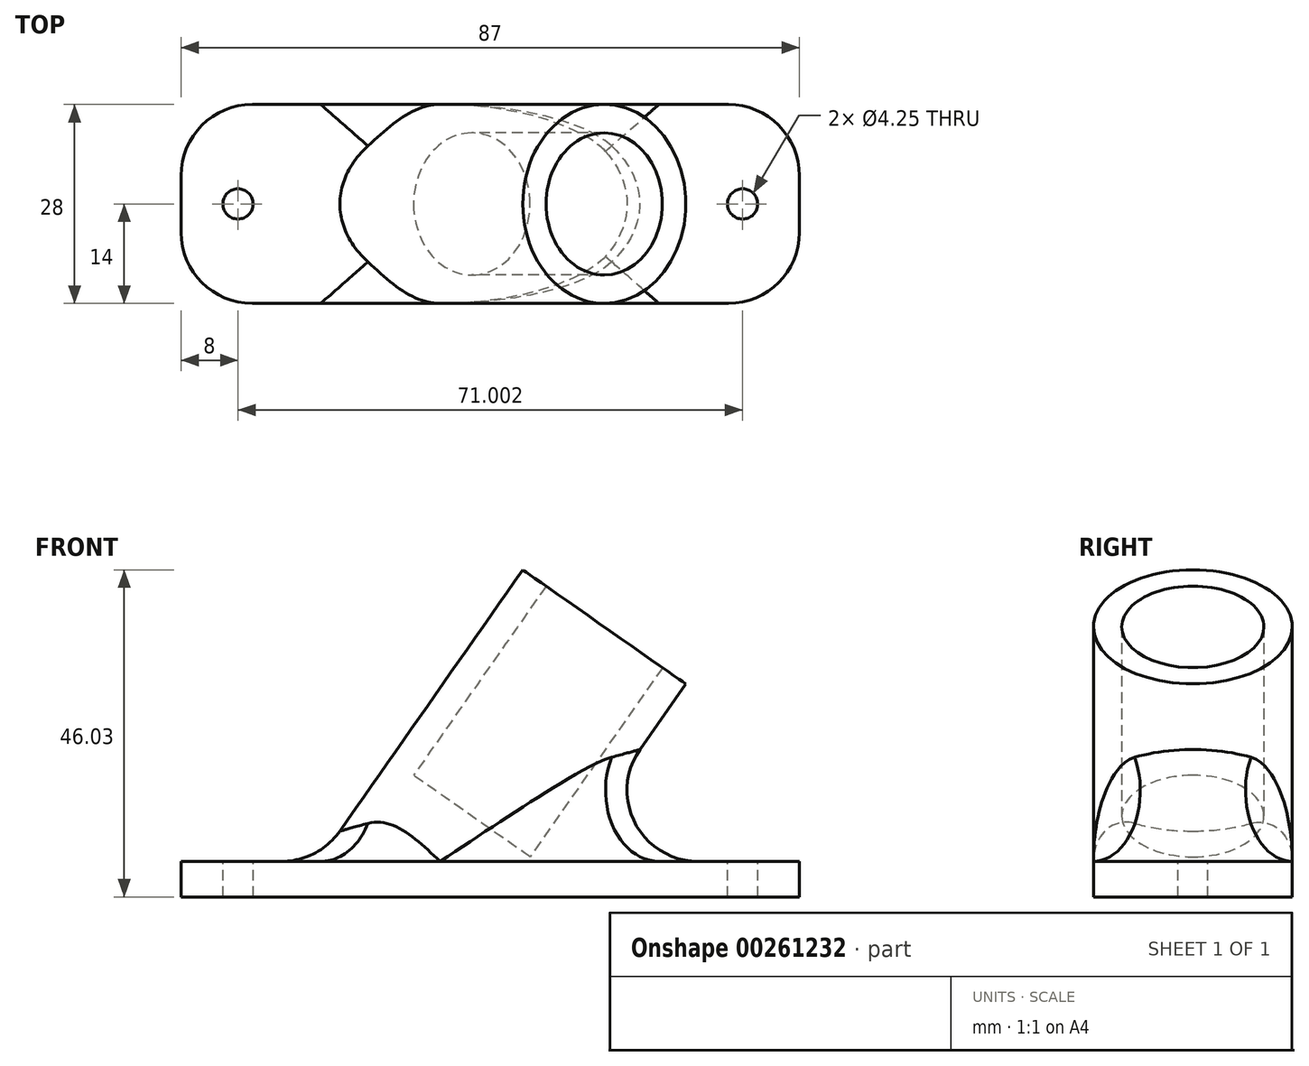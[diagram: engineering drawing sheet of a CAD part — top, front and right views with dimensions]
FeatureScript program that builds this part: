
annotation { "Feature Type Name" : "Feature", "Feature Type Description" : "" }
export const myFeature = defineFeature(function(context is Context, id is Id, definition is map)
    precondition{}
    {
        {
            var Q0;
            Q0=qCreatedBy(makeId("Front.planeOp"),FACE);
            var sketch = newSketch(context, id + "F0", { "sketchPlane" : qUnion([Q0])});
            skPoint(sketch, "E0", {"position": v(-30, 0) * mm});
            skPoint(sketch, "E1", {"position": v(30, 0) * mm});
            skLineSegment(sketch, "E2", {"start": v(-30, 0) * mm, "end": v(30, 0) * mm, "construction": true});
            skLineSegment(sketch, "E3", {"start": v(0, 0) * mm, "end": v(30.9, 44.14) * mm, "construction": true});
            skLineSegment(sketch, "E4", {"start": v(0, 0) * mm, "end": v(0, 38) * mm, "construction": true});
            skLineSegment(sketch, "E5", {"start": v(0, 38) * mm, "end": v(26.6, 38) * mm, "construction": true});
            skPoint(sketch, "E6", {"position": v(26.6, 38) * mm});
            skSolve(sketch);
        }
        {
            var Q0;
            Q0=qCreatedBy(makeId("Front.planeOp"),FACE);
            var sketch = newSketch(context, id + "F1", { "sketchPlane" : qUnion([Q0])});
            skLineSegment(sketch, "E7.0", {"start": v(-30, 0) * mm, "end": v(30, 0) * mm});
            skPoint(sketch, "E8.0", {"position": v(26.6, 38) * mm});
            skLineSegment(sketch, "E9", {"start": v(26.6, 38) * mm, "end": v(38.08, 29.97) * mm, "construction": true});
            skLineSegment(sketch, "E10", {"start": v(26.6, 38) * mm, "end": v(15.14, 46.03) * mm, "construction": true});
            skLineSegment(sketch, "E11", {"start": v(0, 0) * mm, "end": v(0, 5) * mm});
            skLineSegment(sketch, "E12", {"start": v(15.14, 46.03) * mm, "end": v(18.42, 43.74) * mm});
            skLineSegment(sketch, "E13", {"start": v(18.42, 43.74) * mm, "end": v(-15.51, -4.72) * mm});
            skLineSegment(sketch, "E14", {"start": v(-15.51, -4.72) * mm, "end": v(-18.79, -2.42) * mm});
            skLineSegment(sketch, "E15", {"start": v(-18.79, -2.42) * mm, "end": v(15.14, 46.03) * mm});
            skLineSegment(sketch, "E16.0", {"start": v(0, 0) * mm, "end": v(30.9, 44.14) * mm});
            skSolve(sketch);
        }
        {
            var Q0;
            Q0 = qSketchRegion(id + "F1", true);
            var Q1;
            Q1=sQuery(id+"F1.wireOp",EDGE,"E16.0");
            revolve(context, id + "F2", {"entities" : qUnion([Q0]), "axis" : qUnion([Q1]), "revolveType" : RevolveType.FULL});
        }
        {
            var Q0;
            Q0=qCreatedBy(makeId("Top.planeOp"),FACE);
            var sketch = newSketch(context, id + "F3", { "sketchPlane" : qUnion([Q0])});
            skLineSegment(sketch, "E17", {"start": v(38.07, 0) * mm, "end": v(54.07, 0) * mm});
            skLineSegment(sketch, "E18", {"start": v(-16.93, 0) * mm, "end": v(-32.93, 0) * mm});
            skLineSegment(sketch, "E19", {"start": v(-32.93, 0) * mm, "end": v(-32.93, 14) * mm});
            skLineSegment(sketch, "E20", {"start": v(-32.93, 14) * mm, "end": v(54.07, 14) * mm});
            skLineSegment(sketch, "E21", {"start": v(54.07, 14) * mm, "end": v(54.07, -14) * mm});
            skLineSegment(sketch, "E22", {"start": v(54.07, -14) * mm, "end": v(-32.93, -14) * mm});
            skLineSegment(sketch, "E23", {"start": v(-32.93, -14) * mm, "end": v(-32.93, 0) * mm});
            skSolve(sketch);
        }
        {
            var Q0;
            Q0=makeQuery(id+"F3.imprint","IMPRINT",FACE,{"disambiguationData":[TD([[makeQuery(id+"F3.imprint","IMPRINT",EDGE,{"derivedFrom":sQuery(id+"F3.wireOp",EDGE,"E19")}),-1.0]])]});
            extrude(context, id + "F4", {"entities" : qUnion([Q0]), "operationType" : NewBodyOperationType.ADD, "depth" : 5 * mm});
        }
        {
            var Q0;
            Q0=makeQuery(id+"F4.opExtrude","SWEPT_EDGE",EDGE,{"disambiguationData":[OSD([sQuery(id+"F3.wireOp",EDGE,"E19"),sQuery(id+"F3.wireOp",EDGE,"E20")])]});
            var Q1;
            Q1=makeQuery(id+"F4.opExtrude","SWEPT_EDGE",EDGE,{"disambiguationData":[OSD([sQuery(id+"F3.wireOp",EDGE,"E22"),sQuery(id+"F3.wireOp",EDGE,"E23")])]});
            var Q2;
            Q2=makeQuery(id+"F4.opExtrude","SWEPT_EDGE",EDGE,{"disambiguationData":[OSD([sQuery(id+"F3.wireOp",EDGE,"E20"),sQuery(id+"F3.wireOp",EDGE,"E21")])]});
            var Q3;
            Q3=makeQuery(id+"F4.opExtrude","SWEPT_EDGE",EDGE,{"disambiguationData":[OSD([sQuery(id+"F3.wireOp",EDGE,"E21"),sQuery(id+"F3.wireOp",EDGE,"E22")])]});
            fillet(context, id + "F5", {"entities" : qUnion([Q0, Q1, Q2, Q3]), "radius" : 10 * mm, "tangentPropagation" : true, "allowEdgeOverflow" : false});
        }
        {
            var Q0;
            Q0=makeQuery(id+"F4.boolean.opBoolean","INTERSECT",EDGE,{"disambiguationData":[OD(0.0)],"derivedFrom":[makeQuery(id+"F2.opRevolve","SWEPT_FACE",FACE,{"disambiguationData":[OSD([sQuery(id+"F1.wireOp",EDGE,"E15")])]}),makeQuery(id+"F4.opExtrude","CAP_FACE",FACE,{"disambiguationData":[OSD([sQuery(id+"F3.wireOp",EDGE,"E19"),sQuery(id+"F3.wireOp",EDGE,"E20"),sQuery(id+"F3.wireOp",EDGE,"E21"),sQuery(id+"F3.wireOp",EDGE,"E22"),sQuery(id+"F3.wireOp",EDGE,"E23")])],"isStart":false})]});
            fillet(context, id + "F6", {"entities" : qUnion([Q0]), "radius" : 10 * mm, "tangentPropagation" : true, "allowEdgeOverflow" : false});
        }
        {
            var Q0;
            {var subQ0=sQuery(id+"F3.wireOp",EDGE,"E21");var subQ1=sQuery(id+"F3.wireOp",EDGE,"E20");var subQ2=sQuery(id+"F3.wireOp",EDGE,"E22");var subQ3=makeQuery(id+"F4.opExtrude","CAP_FACE",FACE,{"disambiguationData":[OSD([sQuery(id+"F3.wireOp",EDGE,"E19"),subQ1,subQ0,subQ2,sQuery(id+"F3.wireOp",EDGE,"E23")])],"isStart":true});Q0=makeQuery(id+"F4.boolean.opBoolean","SPLIT",FACE,{"disambiguationData":[TD([makeQuery(id+"F4.opExtrude","SWEPT_FACE",FACE,{"disambiguationData":[OSD([subQ0])]})])],"derivedFrom":subQ3});}
            var sketch = newSketch(context, id + "F7", { "sketchPlane" : qUnion([Q0])});
            skLineSegment(sketch, "E24.0", {"start": v(44.07, 14) * mm, "end": v(0, 14) * mm});
            skArc(sketch, "E25.0", {"start": v(54.07, 4) * mm, "mid": v(51.14, 11.07) * mm, "end": v(44.07, 14) * mm});
            skLineSegment(sketch, "E26.0", {"start": v(54.07, -4) * mm, "end": v(54.07, 4) * mm});
            skArc(sketch, "E27.0", {"start": v(44.07, -14) * mm, "mid": v(51.14, -11.07) * mm, "end": v(54.07, -4) * mm});
            skLineSegment(sketch, "E28.0", {"start": v(0, -14) * mm, "end": v(44.07, -14) * mm});
            skLineSegment(sketch, "E29.0", {"start": v(-22.93, -14) * mm, "end": v(0, -14) * mm});
            skArc(sketch, "E30.0", {"start": v(-32.93, -4) * mm, "mid": v(-30, -11.07) * mm, "end": v(-22.93, -14) * mm});
            skLineSegment(sketch, "E31.0", {"start": v(-32.93, 4) * mm, "end": v(-32.93, -4) * mm});
            skArc(sketch, "E32.0", {"start": v(-22.93, 14) * mm, "mid": v(-30, 11.07) * mm, "end": v(-32.93, 4) * mm});
            skLineSegment(sketch, "E33.0", {"start": v(0, 14) * mm, "end": v(-22.93, 14) * mm});
            skSolve(sketch);
        }
        {
            var Q0;
            Q0=makeQuery(id+"F2.opRevolve","SWEPT_FACE",FACE,{"disambiguationData":[OSD([sQuery(id+"F1.wireOp",EDGE,"E12")])]});
            cPlane(context, id + "F8", {"entities" : qUnion([Q0]), "cplaneType" : CPlaneType.OFFSET, "offset" : 32.5 * mm, "oppositeDirection" : true, "width" : 150 * mm, "height" : 150 * mm});
        }
        {
            var Q0;
            Q0=qCreatedBy(id+"F8.planeOp",FACE);
            var sketch = newSketch(context, id + "F9", { "sketchPlane" : qUnion([Q0])});
            skCircle(sketch, "E34", {"center": v(0, 0) * mm, "radius": 11 * mm});
            skSolve(sketch);
        }
        {
            var Q0;
            Q0=makeQuery(id+"F9.imprint","IMPRINT",FACE,{"disambiguationData":[TD([[makeQuery(id+"F9.imprint","IMPRINT",EDGE,{"derivedFrom":sQuery(id+"F9.wireOp",EDGE,"E34")}),1.0]])]});
            extrude(context, id + "F10", {"entities" : qUnion([Q0]), "operationType" : NewBodyOperationType.ADD, "oppositeDirection" : true, "depth" : 20 * mm});
        }
        {
            var Q0;
            Q0 = qSketchRegion(id + "F7", true);
            extrude(context, id + "F11", {"entities" : qUnion([Q0]), "operationType" : NewBodyOperationType.REMOVE, "depth" : 20 * mm});
        }
        {
            var Q0;
            {var subQ0=sQuery(id+"F3.wireOp",EDGE,"E20");var subQ1=sQuery(id+"F3.wireOp",EDGE,"E23");var subQ2=sQuery(id+"F3.wireOp",EDGE,"E19");var subQ3=sQuery(id+"F3.wireOp",EDGE,"E22");var subQ4=makeQuery(id+"F4.opExtrude","CAP_FACE",FACE,{"disambiguationData":[OSD([subQ2,subQ0,sQuery(id+"F3.wireOp",EDGE,"E21"),subQ3,subQ1])],"isStart":false});Q0=makeQuery(id+"F4.boolean.opBoolean","SPLIT",FACE,{"disambiguationData":[TD([makeQuery(id+"F4.opExtrude","SWEPT_FACE",FACE,{"disambiguationData":[OSD([subQ2,subQ1])]})])],"derivedFrom":subQ4});}
            var sketch = newSketch(context, id + "F12", { "sketchPlane" : qUnion([Q0])});
            skLineSegment(sketch, "E35", {"start": v(-32.93, 0) * mm, "end": v(-24.93, 0) * mm});
            skPoint(sketch, "E35.endSnap0", {"position": v(-32.93, 0) * mm});
            skCircle(sketch, "E36", {"center": v(-24.93, 0) * mm, "radius": 2.12 * mm});
            skSolve(sketch);
        }
        {
            var Q0;
            Q0=makeQuery(id+"F12.imprint","IMPRINT",FACE,{"disambiguationData":[TD([[makeQuery(id+"F12.imprint","IMPRINT",EDGE,{"derivedFrom":sQuery(id+"F12.wireOp",EDGE,"E36")}),1.0]])]});
            extrude(context, id + "F13", {"entities" : qUnion([Q0]), "operationType" : NewBodyOperationType.REMOVE, "oppositeDirection" : true, "depth" : 6 * mm});
        }
        {
            var Q0;
            {var subQ0=sQuery(id+"F3.wireOp",EDGE,"E21");var subQ1=sQuery(id+"F3.wireOp",EDGE,"E20");var subQ2=sQuery(id+"F3.wireOp",EDGE,"E22");var subQ3=makeQuery(id+"F4.opExtrude","CAP_FACE",FACE,{"disambiguationData":[OSD([sQuery(id+"F3.wireOp",EDGE,"E19"),subQ1,subQ0,subQ2,sQuery(id+"F3.wireOp",EDGE,"E23")])],"isStart":false});Q0=makeQuery(id+"F4.boolean.opBoolean","SPLIT",FACE,{"disambiguationData":[TD([makeQuery(id+"F4.opExtrude","SWEPT_FACE",FACE,{"disambiguationData":[OSD([subQ0])]})])],"derivedFrom":subQ3});}
            var sketch = newSketch(context, id + "F14", { "sketchPlane" : qUnion([Q0])});
            skPoint(sketch, "E37.endSnap0", {"position": v(54.07, 0) * mm});
            skCircle(sketch, "E38", {"center": v(46.07, 0) * mm, "radius": 2.12 * mm});
            skSolve(sketch);
        }
        {
            var Q0;
            Q0=makeQuery(id+"F14.imprint","IMPRINT",FACE,{"disambiguationData":[TD([[makeQuery(id+"F14.imprint","IMPRINT",EDGE,{"derivedFrom":sQuery(id+"F14.wireOp",EDGE,"E38")}),1.0]])]});
            extrude(context, id + "F15", {"entities" : qUnion([Q0]), "operationType" : NewBodyOperationType.REMOVE, "oppositeDirection" : true, "depth" : 6 * mm});
        }
    });
